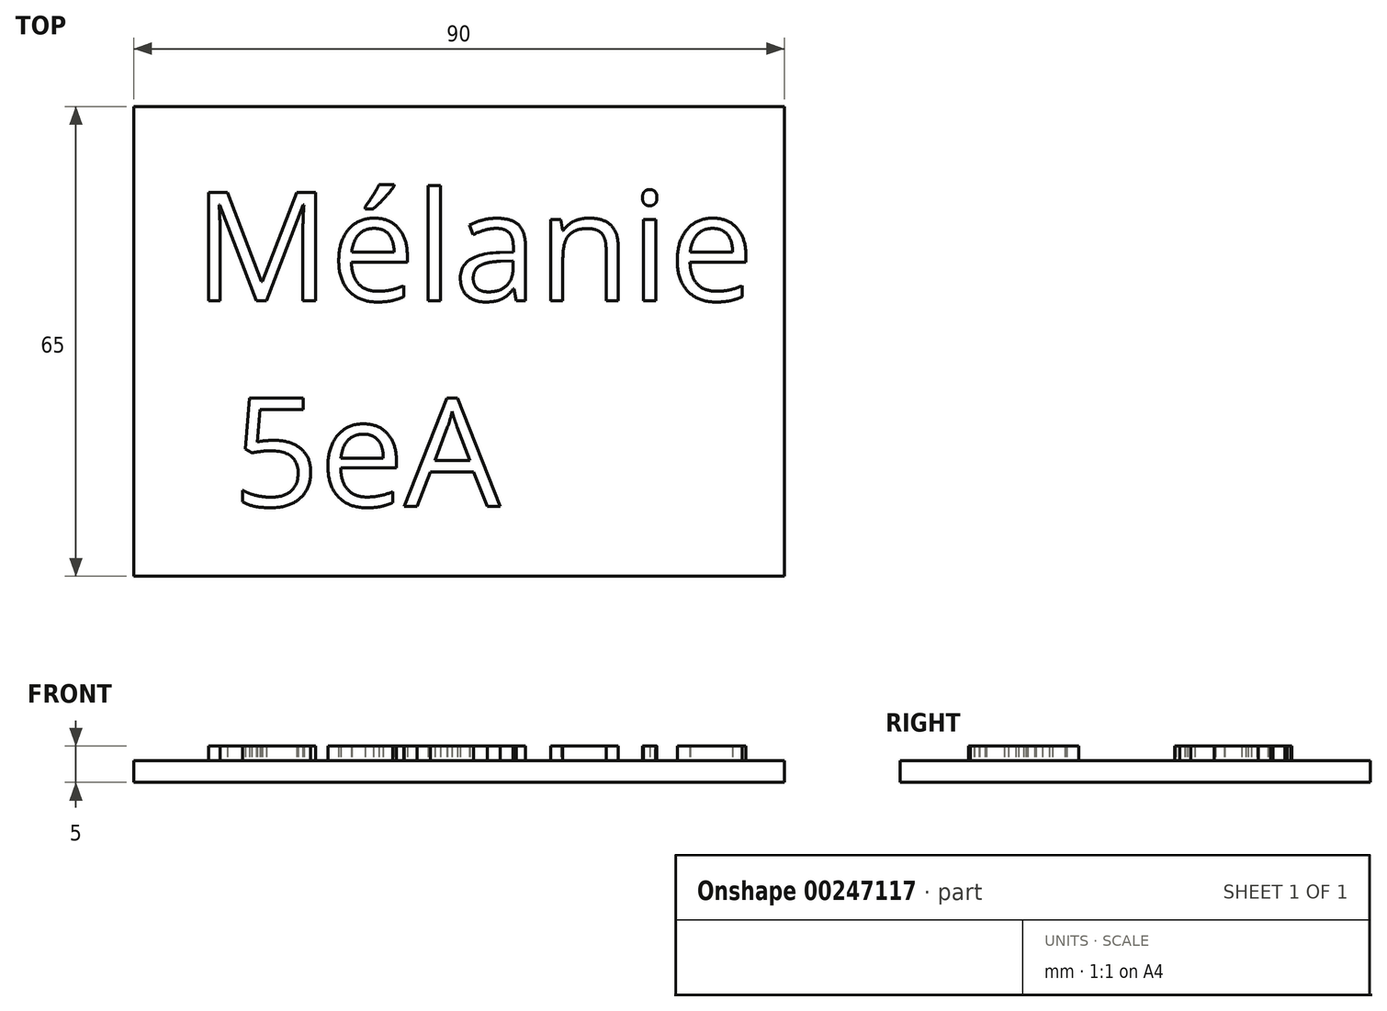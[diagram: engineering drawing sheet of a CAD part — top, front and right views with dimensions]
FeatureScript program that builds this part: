
annotation { "Feature Type Name" : "Feature", "Feature Type Description" : "" }
export const myFeature = defineFeature(function(context is Context, id is Id, definition is map)
    precondition{}
    {
        {
            var Q0;
            Q0=qCreatedBy(makeId("Top.planeOp"),FACE);
            var sketch = newSketch(context, id + "F0", { "sketchPlane" : qUnion([Q0])});
            skLineSegment(sketch, "E0.bottom", {"start": v(0, 0) * mm, "end": v(90, 0) * mm});
            skLineSegment(sketch, "E0.top", {"start": v(0, -65) * mm, "end": v(90, -65) * mm});
            skLineSegment(sketch, "E0.left", {"start": v(0, 0) * mm, "end": v(0, -65) * mm});
            skLineSegment(sketch, "E0.right", {"start": v(90, 0) * mm, "end": v(90, -65) * mm});
            skSolve(sketch);
        }
        {
            var Q0;
            Q0 = qSketchRegion(id + "F0", true);
            extrude(context, id + "F1", {"entities" : qUnion([Q0]), "depth" : 3 * mm});
        }
        {
            var Q0;
            Q0=makeQuery(id+"F1.opExtrude","CAP_FACE",FACE,{"disambiguationData":[OSD([sQuery(id+"F0.wireOp",EDGE,"E0.bottom"),sQuery(id+"F0.wireOp",EDGE,"E0.top"),sQuery(id+"F0.wireOp",EDGE,"E0.left"),sQuery(id+"F0.wireOp",EDGE,"E0.right")])],"isStart":false});
            var sketch = newSketch(context, id + "F2", { "sketchPlane" : qUnion([Q0])});
            skText(sketch, "E1", { "text": "Mélanie\n 5eA", "fontName": "OpenSans-Regular.ttf"});
            const initialGuessF2  = {"E1": [0.00829, -0.02685, 1, 0, 0.01507]};
            skSetInitialGuess(sketch, initialGuessF2);
            skSolve(sketch);
        }
        {
            var Q0;
            Q0 = qSketchRegion(id + "F2", true);
            extrude(context, id + "F3", {"entities" : qUnion([Q0]), "operationType" : NewBodyOperationType.ADD, "depth" : 2 * mm});
        }
    });
